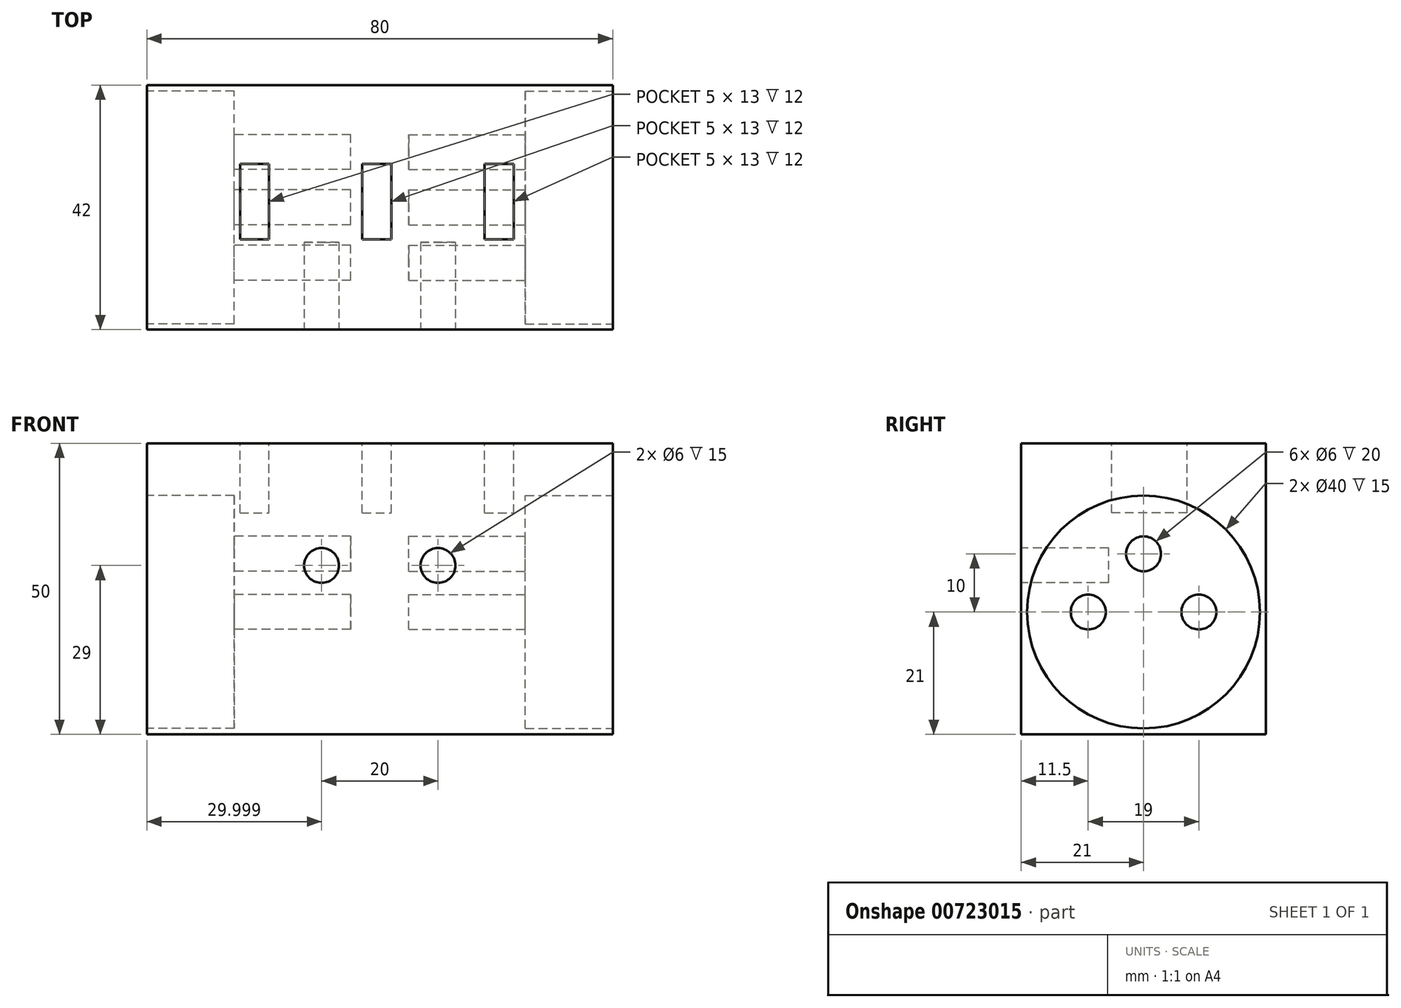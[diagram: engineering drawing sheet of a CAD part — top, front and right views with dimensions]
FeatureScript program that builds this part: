
annotation { "Feature Type Name" : "Feature", "Feature Type Description" : "" }
export const myFeature = defineFeature(function(context is Context, id is Id, definition is map)
    precondition{}
    {
        {
            var Q0;
            Q0=qCreatedBy(makeId("Top.planeOp"),FACE);
            var sketch = newSketch(context, id + "F0", { "sketchPlane" : qUnion([Q0])});
            skLineSegment(sketch, "E0.bottom", {"start": v(2.42, 0) * mm, "end": v(82.42, 0) * mm});
            skLineSegment(sketch, "E0.top", {"start": v(2.42, -42) * mm, "end": v(82.42, -42) * mm});
            skLineSegment(sketch, "E0.left", {"start": v(2.42, 0) * mm, "end": v(2.42, -42) * mm});
            skLineSegment(sketch, "E0.right", {"start": v(82.42, 0) * mm, "end": v(82.42, -42) * mm});
            skSolve(sketch);
        }
        {
            var Q0;
            Q0 = qSketchRegion(id + "F0", true);
            extrude(context, id + "F1", {"entities" : qUnion([Q0]), "depth" : 50 * mm, "offsetDistance" : 25 * mm});
        }
        {
            var Q0;
            Q0=makeQuery(id+"F1.opExtrude","CAP_FACE",FACE,{"disambiguationData":[OSD([sQuery(id+"F0.wireOp",EDGE,"E0.bottom"),sQuery(id+"F0.wireOp",EDGE,"E0.top"),sQuery(id+"F0.wireOp",EDGE,"E0.left"),sQuery(id+"F0.wireOp",EDGE,"E0.right")])],"isStart":false});
            var sketch = newSketch(context, id + "F2", { "sketchPlane" : qUnion([Q0])});
            skLineSegment(sketch, "E1.bottom", {"start": v(18.42, -13.5) * mm, "end": v(23.42, -13.5) * mm});
            skLineSegment(sketch, "E1.top", {"start": v(18.42, -26.5) * mm, "end": v(23.42, -26.5) * mm});
            skLineSegment(sketch, "E1.left", {"start": v(18.42, -13.5) * mm, "end": v(18.42, -26.5) * mm});
            skLineSegment(sketch, "E1.right", {"start": v(23.42, -13.5) * mm, "end": v(23.42, -26.5) * mm});
            skSolve(sketch);
        }
        {
            var Q0;
            Q0 = qSketchRegion(id + "F2", true);
            extrude(context, id + "F3", {"entities" : qUnion([Q0]), "operationType" : NewBodyOperationType.REMOVE, "oppositeDirection" : true, "depth" : 12 * mm, "offsetDistance" : 25 * mm});
        }
        {
            var Q0;
            Q0=makeQuery(id+"F1.opExtrude","CAP_FACE",FACE,{"disambiguationData":[OSD([sQuery(id+"F0.wireOp",EDGE,"E0.bottom"),sQuery(id+"F0.wireOp",EDGE,"E0.top"),sQuery(id+"F0.wireOp",EDGE,"E0.left"),sQuery(id+"F0.wireOp",EDGE,"E0.right")])],"isStart":false});
            var sketch = newSketch(context, id + "F4", { "sketchPlane" : qUnion([Q0])});
            skLineSegment(sketch, "E2.bottom", {"start": v(39.42, -13.5) * mm, "end": v(44.42, -13.5) * mm});
            skLineSegment(sketch, "E2.top", {"start": v(39.42, -26.5) * mm, "end": v(44.42, -26.5) * mm});
            skLineSegment(sketch, "E2.left", {"start": v(39.42, -13.5) * mm, "end": v(39.42, -26.5) * mm});
            skLineSegment(sketch, "E2.right", {"start": v(44.42, -13.5) * mm, "end": v(44.42, -26.5) * mm});
            skSolve(sketch);
        }
        {
            var Q0;
            Q0 = qSketchRegion(id + "F4", true);
            extrude(context, id + "F5", {"entities" : qUnion([Q0]), "operationType" : NewBodyOperationType.REMOVE, "oppositeDirection" : true, "depth" : 12 * mm, "offsetDistance" : 25 * mm});
        }
        {
            var Q0;
            Q0=makeQuery(id+"F1.opExtrude","CAP_FACE",FACE,{"disambiguationData":[OSD([sQuery(id+"F0.wireOp",EDGE,"E0.bottom"),sQuery(id+"F0.wireOp",EDGE,"E0.top"),sQuery(id+"F0.wireOp",EDGE,"E0.left"),sQuery(id+"F0.wireOp",EDGE,"E0.right")])],"isStart":false});
            var sketch = newSketch(context, id + "F6", { "sketchPlane" : qUnion([Q0])});
            skPoint(sketch, "E3.firstSnap0", {"position": v(41.92, -13.5) * mm});
            skLineSegment(sketch, "E3.bottom", {"start": v(60.42, -13.5) * mm, "end": v(65.42, -13.5) * mm});
            skLineSegment(sketch, "E3.top", {"start": v(60.42, -26.5) * mm, "end": v(65.42, -26.5) * mm});
            skLineSegment(sketch, "E3.left", {"start": v(60.42, -13.5) * mm, "end": v(60.42, -26.5) * mm});
            skLineSegment(sketch, "E3.right", {"start": v(65.42, -13.5) * mm, "end": v(65.42, -26.5) * mm});
            skSolve(sketch);
        }
        {
            var Q0;
            Q0 = qSketchRegion(id + "F6", true);
            extrude(context, id + "F7", {"entities" : qUnion([Q0]), "operationType" : NewBodyOperationType.REMOVE, "oppositeDirection" : true, "depth" : 12 * mm, "offsetDistance" : 25 * mm});
        }
        {
            var Q0;
            Q0=makeQuery(id+"F1.opExtrude","SWEPT_FACE",FACE,{"disambiguationData":[OSD([sQuery(id+"F0.wireOp",EDGE,"E0.right")])]});
            var sketch = newSketch(context, id + "F8", { "sketchPlane" : qUnion([Q0])});
            skCircle(sketch, "E4", {"center": v(-21, 21) * mm, "radius": 20 * mm});
            skSolve(sketch);
        }
        {
            var Q0;
            Q0 = qSketchRegion(id + "F8", true);
            extrude(context, id + "F9", {"entities" : qUnion([Q0]), "operationType" : NewBodyOperationType.REMOVE, "oppositeDirection" : true, "depth" : 15 * mm, "offsetDistance" : 25 * mm});
        }
        {
            var Q0;
            Q0=makeQuery(id+"F9.boolean.opBoolean","COPY",FACE,{"derivedFrom":makeQuery(id+"F9.opExtrude","CAP_FACE",FACE,{"disambiguationData":[OSD([sQuery(id+"F8.wireOp",EDGE,"E4")])],"isStart":false})});
            var sketch = newSketch(context, id + "F10", { "sketchPlane" : qUnion([Q0])});
            skCircle(sketch, "E5", {"center": v(-11.5, 21) * mm, "radius": 3 * mm});
            skSolve(sketch);
        }
        {
            var Q0;
            Q0 = qSketchRegion(id + "F10", true);
            extrude(context, id + "F11", {"entities" : qUnion([Q0]), "operationType" : NewBodyOperationType.REMOVE, "oppositeDirection" : true, "depth" : 20 * mm, "offsetDistance" : 25 * mm});
        }
        {
            var Q0;
            Q0=makeQuery(id+"F9.boolean.opBoolean","COPY",FACE,{"derivedFrom":makeQuery(id+"F9.opExtrude","CAP_FACE",FACE,{"disambiguationData":[OSD([sQuery(id+"F8.wireOp",EDGE,"E4")])],"isStart":false})});
            var sketch = newSketch(context, id + "F12", { "sketchPlane" : qUnion([Q0])});
            skCircle(sketch, "E6", {"center": v(-30.5, 21) * mm, "radius": 3 * mm});
            skSolve(sketch);
        }
        {
            var Q0;
            Q0 = qSketchRegion(id + "F12", true);
            extrude(context, id + "F13", {"entities" : qUnion([Q0]), "operationType" : NewBodyOperationType.REMOVE, "oppositeDirection" : true, "depth" : 20 * mm, "offsetDistance" : 25 * mm});
        }
        {
            var Q0;
            Q0=makeQuery(id+"F9.boolean.opBoolean","COPY",FACE,{"derivedFrom":makeQuery(id+"F9.opExtrude","CAP_FACE",FACE,{"disambiguationData":[OSD([sQuery(id+"F8.wireOp",EDGE,"E4")])],"isStart":false})});
            var sketch = newSketch(context, id + "F14", { "sketchPlane" : qUnion([Q0])});
            skCircle(sketch, "E7", {"center": v(-21, 31) * mm, "radius": 3 * mm});
            skSolve(sketch);
        }
        {
            var Q0;
            Q0 = qSketchRegion(id + "F14", true);
            extrude(context, id + "F15", {"entities" : qUnion([Q0]), "operationType" : NewBodyOperationType.REMOVE, "oppositeDirection" : true, "depth" : 20 * mm, "offsetDistance" : 25 * mm});
        }
        {
            var Q0;
            Q0=makeQuery(id+"F1.opExtrude","SWEPT_FACE",FACE,{"disambiguationData":[OSD([sQuery(id+"F0.wireOp",EDGE,"E0.left")])]});
            var sketch = newSketch(context, id + "F16", { "sketchPlane" : qUnion([Q0])});
            skCircle(sketch, "E8", {"center": v(21, 21) * mm, "radius": 20 * mm});
            skSolve(sketch);
        }
        {
            var Q0;
            Q0 = qSketchRegion(id + "F16", true);
            extrude(context, id + "F17", {"entities" : qUnion([Q0]), "operationType" : NewBodyOperationType.REMOVE, "oppositeDirection" : true, "depth" : 15 * mm, "offsetDistance" : 25 * mm});
        }
        {
            var Q0;
            Q0=makeQuery(id+"F17.boolean.opBoolean","COPY",FACE,{"derivedFrom":makeQuery(id+"F17.opExtrude","CAP_FACE",FACE,{"disambiguationData":[OSD([sQuery(id+"F16.wireOp",EDGE,"E8")])],"isStart":false})});
            var sketch = newSketch(context, id + "F18", { "sketchPlane" : qUnion([Q0])});
            skCircle(sketch, "E9", {"center": v(30.5, 21) * mm, "radius": 3 * mm});
            skSolve(sketch);
        }
        {
            var Q0;
            Q0 = qSketchRegion(id + "F18", true);
            extrude(context, id + "F19", {"entities" : qUnion([Q0]), "operationType" : NewBodyOperationType.REMOVE, "oppositeDirection" : true, "depth" : 20 * mm, "offsetDistance" : 25 * mm});
        }
        {
            var Q0;
            Q0=makeQuery(id+"F17.boolean.opBoolean","COPY",FACE,{"derivedFrom":makeQuery(id+"F17.opExtrude","CAP_FACE",FACE,{"disambiguationData":[OSD([sQuery(id+"F16.wireOp",EDGE,"E8")])],"isStart":false})});
            var sketch = newSketch(context, id + "F20", { "sketchPlane" : qUnion([Q0])});
            skCircle(sketch, "E10", {"center": v(11.5, 21) * mm, "radius": 3 * mm});
            skSolve(sketch);
        }
        {
            var Q0;
            Q0 = qSketchRegion(id + "F20", true);
            extrude(context, id + "F21", {"entities" : qUnion([Q0]), "operationType" : NewBodyOperationType.REMOVE, "oppositeDirection" : true, "depth" : 20 * mm, "offsetDistance" : 25 * mm});
        }
        {
            var Q0;
            Q0=makeQuery(id+"F17.boolean.opBoolean","COPY",FACE,{"derivedFrom":makeQuery(id+"F17.opExtrude","CAP_FACE",FACE,{"disambiguationData":[OSD([sQuery(id+"F16.wireOp",EDGE,"E8")])],"isStart":false})});
            var sketch = newSketch(context, id + "F22", { "sketchPlane" : qUnion([Q0])});
            skCircle(sketch, "E11", {"center": v(21, 31) * mm, "radius": 3 * mm});
            skSolve(sketch);
        }
        {
            var Q0;
            Q0 = qSketchRegion(id + "F22", true);
            extrude(context, id + "F23", {"entities" : qUnion([Q0]), "operationType" : NewBodyOperationType.REMOVE, "oppositeDirection" : true, "depth" : 20 * mm, "offsetDistance" : 25 * mm});
        }
        {
            var Q0;
            Q0=makeQuery(id+"F1.opExtrude","SWEPT_FACE",FACE,{"disambiguationData":[OSD([sQuery(id+"F0.wireOp",EDGE,"E0.top")])]});
            var sketch = newSketch(context, id + "F24", { "sketchPlane" : qUnion([Q0])});
            skCircle(sketch, "E12", {"center": v(32.42, 29) * mm, "radius": 3 * mm});
            skSolve(sketch);
        }
        {
            var Q0;
            Q0 = qSketchRegion(id + "F24", true);
            extrude(context, id + "F25", {"entities" : qUnion([Q0]), "operationType" : NewBodyOperationType.REMOVE, "oppositeDirection" : true, "depth" : 15 * mm, "offsetDistance" : 25 * mm});
        }
        {
            var Q0;
            Q0=makeQuery(id+"F1.opExtrude","SWEPT_FACE",FACE,{"disambiguationData":[OSD([sQuery(id+"F0.wireOp",EDGE,"E0.top")])]});
            var sketch = newSketch(context, id + "F26", { "sketchPlane" : qUnion([Q0])});
            skCircle(sketch, "E13", {"center": v(52.42, 29) * mm, "radius": 3 * mm});
            skSolve(sketch);
        }
        {
            var Q0;
            Q0 = qSketchRegion(id + "F26", true);
            extrude(context, id + "F27", {"entities" : qUnion([Q0]), "operationType" : NewBodyOperationType.REMOVE, "oppositeDirection" : true, "depth" : 15 * mm, "offsetDistance" : 25 * mm});
        }
    });
